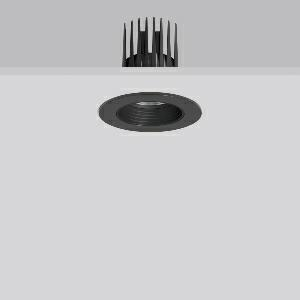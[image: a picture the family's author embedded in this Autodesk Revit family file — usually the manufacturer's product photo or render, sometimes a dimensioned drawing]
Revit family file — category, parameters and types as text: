
# Revit family: heledon_mini_e_901744_003_3_76_87ab
name_source: partatom
category: Lighting Fixtures
units: mm (PartAtom-declared; Revit-internal decimal feet)

## family parameters
Cut with Voids When Loaded = No
Host = Face
Light Source = No
Part Type = Normal
Room Calculation Point = No
Round Connector Dimension = Use Diameter
Shared = No

## types (1)
- HELEDON mini E (1 x LED Modul 935, 2150 lm, 3500)
    Apparent Load = 20 VA
    Approval mark = CE
    CIE Flux Codes = 96 100 100 100 100
    Color Rendering = 92
    Color Temperature = 3500
    Default Elevation = 1800 mm
    Description = Series: HELEDON mini
Round recessed downlight. Housing: die-cast aluminium, powder-coated. Black plastic ring and recessed LED to prevent glare from the side. Optical assembly with lens made of plastic (polycarbonate) for the best homogeneous light distribution - can be changed without tools. Best colour rendering index Ra>90. Suitable for Recessed ceiling mounting. Installation without tools thanks to spring fastening system. Including separate LED converter with connecting cable 600 mm.High quality converter without flickering and stroboscopic effect. Through-wiring box (5 pole) available as accessory. The following accessories can be mounted without use of tools: interchangeable lenses, decorative glasses, honeycomb louvre, clear and frosted diffusers, white interchangeable plastic ring. 
Colour: deep black, matt (RAL 9005)
Diameter: 124 mm
Height: 3 mm
Cut-out diameter: 114 mm
Recess height: 170 mm
Luminaire: recess height: 120 mm
Lamp: LED
Socket: without socket
Colour temperature: 3500K
Colour rendering index (CRI): 92
System power: 20 W
Rated luminous flux: 2150 lm
Luminous efficiency: 108 lm/W
Control gear: Converter, dimmable, DALI
Protection class: II
Type of protection: IP 20
    Height = 0 mm  [stored 0 ft]
    Lamp = 1 x LED Modul 935
    Lamp Light Flux = 2150 lm
    Lamp count = 1
    Length = 124 mm  [stored 0.406824 ft]
    Lifetime = 50000 h
    Luminous efficacy = 108 lm/W
    Manufacturer = RZB
    ModVariant = No
    Model = 901744.003.3.76
    Mounting Place = Ceiling
    Mounting Type = Recessed
    Number of Poles = 1
    OnlyDefault = Yes
    Power Factor = 1
    Product Name = HELEDON mini E
    Product group = Recessed downlights
    ProductGroupID = 402
    Protection Class = Protection class II
    Protection Degree = IP 20
    RLX_Detail_Level = 1
    RLX_Emergency_Light_Flux = 0 lm
    RLX_Emergency_Type = 0
    RLX_Emergency_Type_DB = No
    RlxData = <blob elided: 125597 chars, md5=068013b5>
    Socket = socket
    Standby Power = 0 W
    System Light Flux = 2150 lm
    System Power = 20 W
    Type Comments = Product without accessories
    Type Image = 901656.003.jpg
    URL = http://relux.com
    VarID = ---
    Voltage = 230 V
    Voltage Range = 220-240 V
    Weight = 0.00 kg
    Width = 0 mm  [stored 0 ft]

note: [stored X ft] marks values corroborated as IEEE doubles in the binary element streams (Revit-internal decimal feet)

## geometry (parser evidence)
native form markers: Blend x4, Sweep x10
no freeform markers — native parametric forms only
